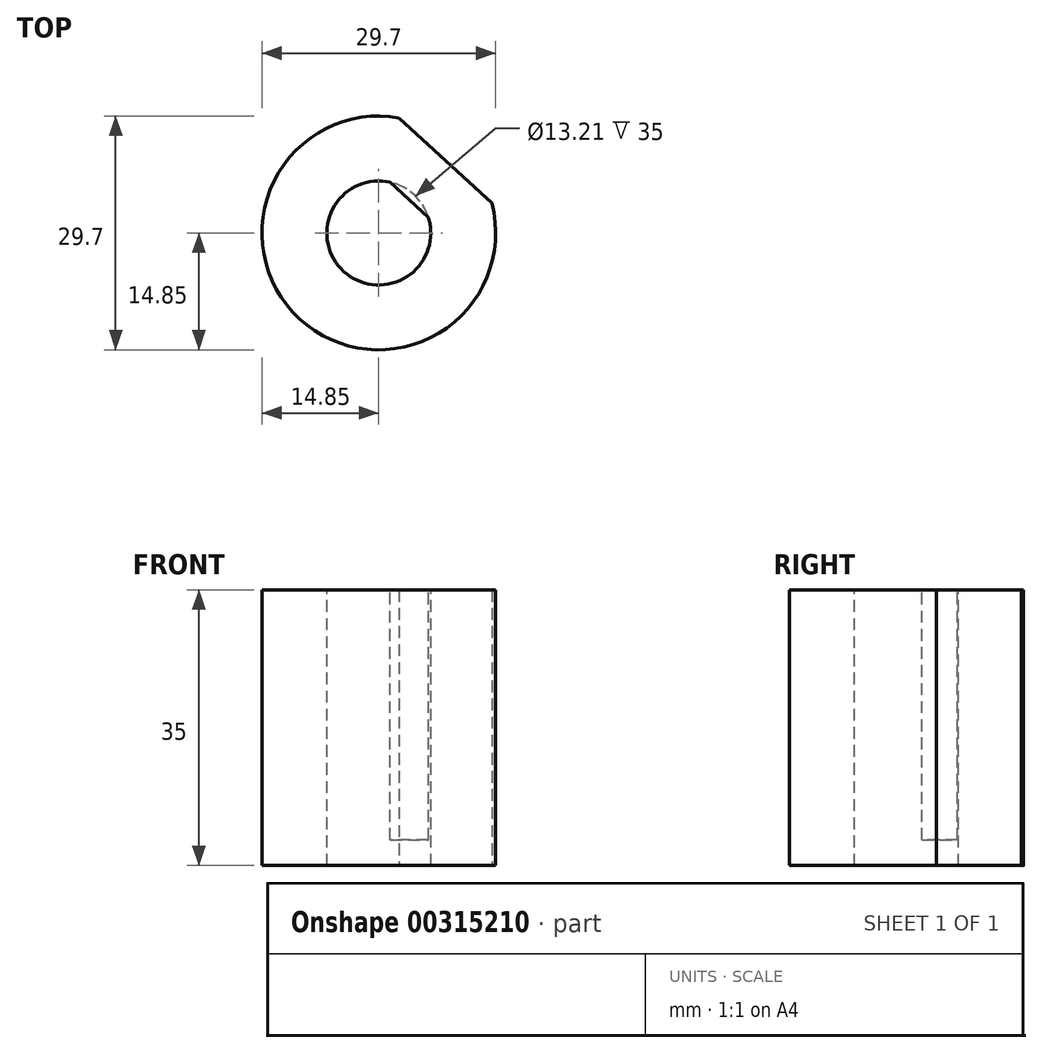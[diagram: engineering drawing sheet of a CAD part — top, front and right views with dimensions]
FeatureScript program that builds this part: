
annotation { "Feature Type Name" : "Feature", "Feature Type Description" : "" }
export const myFeature = defineFeature(function(context is Context, id is Id, definition is map)
    precondition{}
    {
        {
            var Q0;
            Q0=qCreatedBy(makeId("Top.planeOp"),FACE);
            var sketch = newSketch(context, id + "F0", { "sketchPlane" : qUnion([Q0])});
            skLineSegment(sketch, "E0.0", {"start": v(2.6, 14.62) * mm, "end": v(14.36, 3.77) * mm});
            skArc(sketch, "E0.1", {"start": v(2.6, 14.62) * mm, "mid": v(-10.07, -10.92) * mm, "end": v(14.36, 3.77) * mm});
            skSolve(sketch);
        }
        {
            var Q0;
            Q0 = qSketchRegion(id + "F0", true);
            extrude(context, id + "F1", {"entities" : qUnion([Q0]), "depth" : 35 * mm});
        }
        {
            var Q0;
            Q0=makeQuery(id+"F1.opExtrude","CAP_FACE",FACE,{"disambiguationData":[OSD([sQuery(id+"F0.wireOp",EDGE,"E0.0"),sQuery(id+"F0.wireOp",EDGE,"E0.1")])],"isStart":false});
            var sketch = newSketch(context, id + "F2", { "sketchPlane" : qUnion([Q0])});
            skCircle(sketch, "E1", {"center": v(0, 0) * mm, "radius": 6.6 * mm});
            skSolve(sketch);
        }
        {
            var Q0;
            Q0 = qSketchRegion(id + "F2", true);
            extrude(context, id + "F3", {"entities" : qUnion([Q0]), "operationType" : NewBodyOperationType.REMOVE, "oppositeDirection" : true, "depth" : 38.1 * mm});
        }
        {
            var Q0;
            Q0=makeQuery(id+"F1.opExtrude","CAP_FACE",FACE,{"disambiguationData":[OSD([sQuery(id+"F0.wireOp",EDGE,"E0.0"),sQuery(id+"F0.wireOp",EDGE,"E0.1")])],"isStart":false});
            var sketch = newSketch(context, id + "F4", { "sketchPlane" : qUnion([Q0])});
            skLineSegment(sketch, "E2", {"start": v(1.45, 6.44) * mm, "end": v(6.3, 1.97) * mm});
            skSolve(sketch);
        }
        {
            var Q0;
            Q0 = qSketchRegion(id + "F4", true);
            var Q1;
            {var subQ0=sQuery(id+"F4.wireOp",EDGE,"10QnyZcH-7dmd-xprj-wD6r-NXgKqi7b0ndA");Q1=makeQuery(id+"F4.imprint","IMPRINT",FACE,{"disambiguationData":[TD([[makeQuery(id+"F4.imprint","IMPRINT",EDGE,{"derivedFrom":subQ0}),-1.0]])]});}
            var Q2;
            {var subQ0=sQuery(id+"F4.wireOp",EDGE,"E2");Q2=makeQuery(id+"F4.imprint","IMPRINT",FACE,{"disambiguationData":[TD([[makeQuery(id+"F4.imprint","IMPRINT",EDGE,{"derivedFrom":subQ0}),1.0]])]});}
            extrude(context, id + "F5", {"entities" : qUnion([Q0, Q1, Q2]), "operationType" : NewBodyOperationType.ADD, "oppositeDirection" : true, "depth" : 31.75 * mm});
        }
    });
